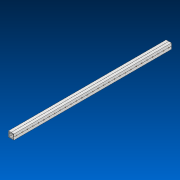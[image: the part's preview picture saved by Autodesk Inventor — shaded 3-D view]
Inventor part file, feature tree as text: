
AUTODESK INVENTOR PART (.ipt)
format: ipt  version: 2022.2 (Build 262287000, 287)  size: 758,784 bytes
history: native  units: in
note: dims shown in document units (in); Inventor stores cm internally (conversion verified against a paired STEP export)
features: other x29, extrude x1, pattern_linear x1, sketch x1, pattern_circular x1
ambient origin geometry x8: Origin, YZ Plane, XZ Plane, XY Plane, X Axis, Y Axis, Z Axis, Center Point
bodies: Solid1 (feature_tree)
feature tree (33):
  extrude  "Extrusion1"  Depth=1.0in
  other  "Work Axis1"
  pattern_linear  "Rectangular Pattern1"  Spacing1=0.0in  [1 undecoded]
  sketch  "Sketch1"  dims[d0=1.0in d1=30.0in d2=0.0in d3=11.4173in d5=1.0in]
  other  "Work Axis2"
  other  "Work Axis3"
  other  "Work Axis4"
  other  "Work Axis5"
  other  "Work Axis6"
  other  "Work Axis7"
  other  "Work Axis8"
  other  "Work Axis9"
  other  "Work Axis10"
  other  "Work Axis11"
  other  "Work Axis12"
  other  "Work Axis13"
  other  "Work Axis14"
  other  "Work Axis15"
  other  "Work Axis16"
  other  "Work Axis17"
  other  "Work Axis18"
  other  "Work Axis19"
  other  "Work Axis20"
  other  "Work Axis21"
  other  "Work Axis22"
  other  "Work Axis23"
  other  "Work Axis24"
  other  "Work Axis25"
  other  "Work Axis26"
  other  "Work Axis27"
  other  "Work Axis28"
  other  "Work Axis29"
  pattern_circular  "CirPattern2"
note: 1 required parameter value undecoded (feature->parameter linkage not recoverable at this tier; creation-order binding heuristic only, values carry confidence <= 0.55)
